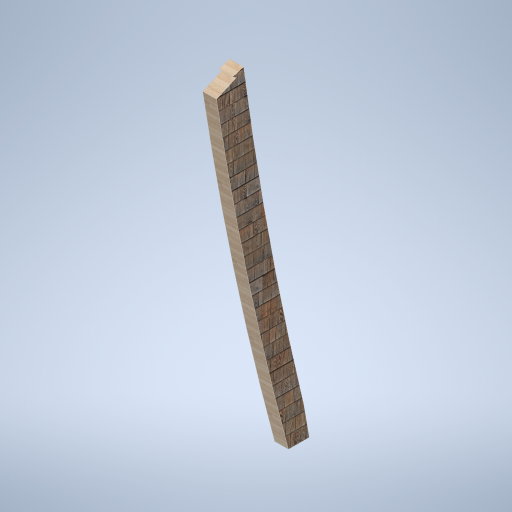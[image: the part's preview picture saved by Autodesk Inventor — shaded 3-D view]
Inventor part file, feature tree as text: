
AUTODESK INVENTOR PART (.ipt)
format: ipt  version: 2024.2 (Build 282272000, 272)  size: 316,928 bytes
history: native  units: in
note: dims shown in document units (in); Inventor stores cm internally (conversion verified against a paired STEP export)
features: other x3, sketch x1
ambient origin geometry x8: Origin, YZ Plane, XZ Plane, XY Plane, X Axis, Y Axis, Z Axis, Center Point
bodies: Solid1 (feature_tree)
feature tree (4):
  other  "side_curve_beam_02_MIR.ipt"
  other  "Solid1::side_curve_beam_02_MIR.ipt"
  other  "TaggingFeature1"
  sketch  "Sketch1"  dims[d0=0.3937in]
